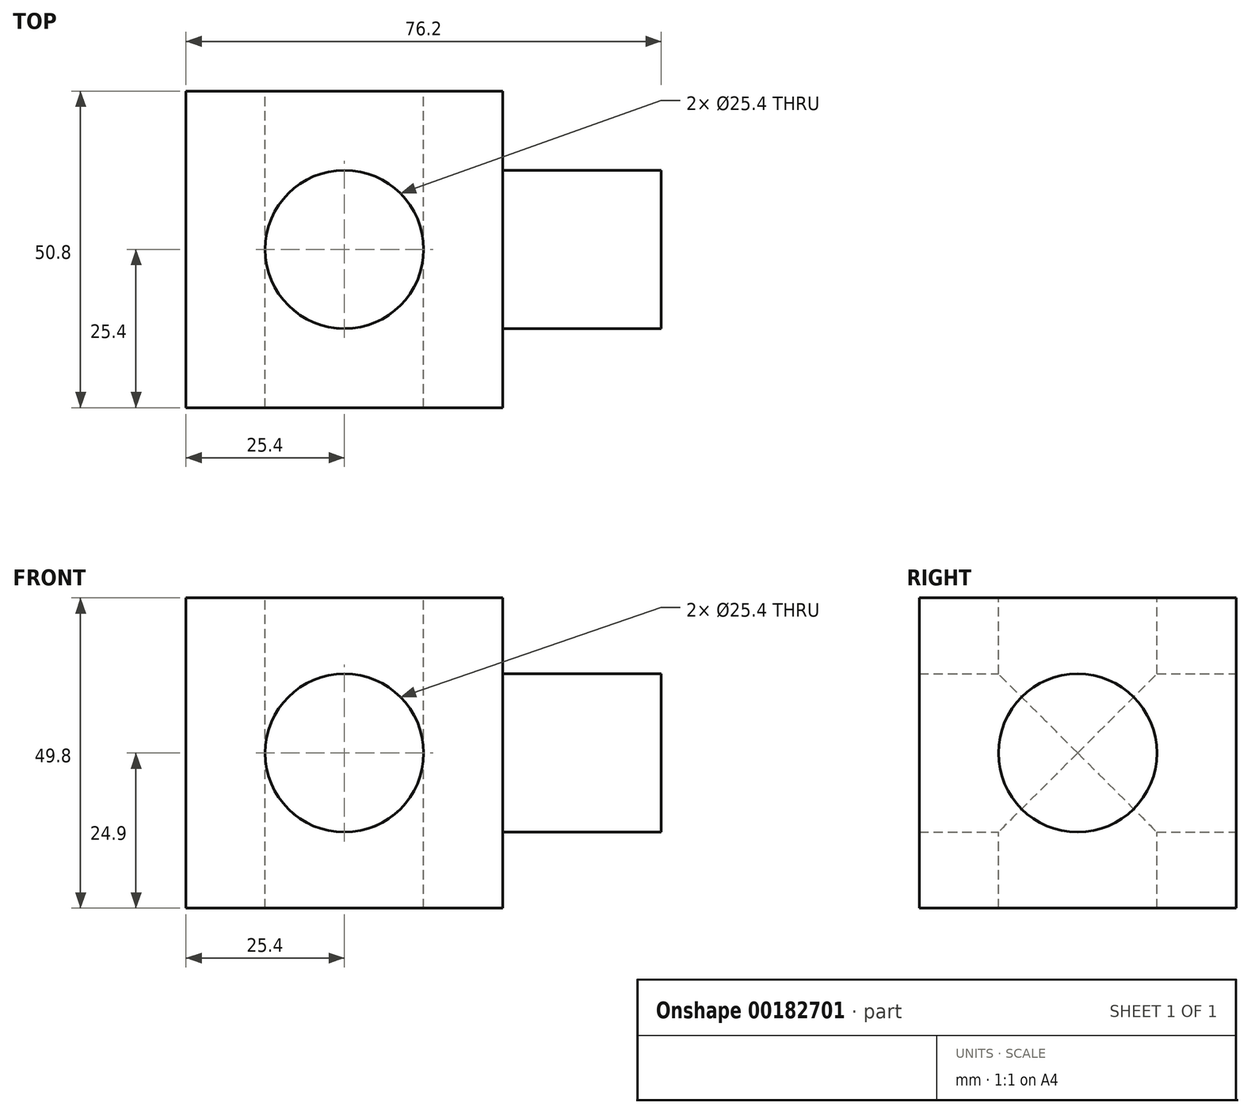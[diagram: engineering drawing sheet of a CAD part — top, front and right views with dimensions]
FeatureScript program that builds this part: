
annotation { "Feature Type Name" : "Feature", "Feature Type Description" : "" }
export const myFeature = defineFeature(function(context is Context, id is Id, definition is map)
    precondition{}
    {
        {
            var Q0;
            Q0=qCreatedBy(makeId("Front.planeOp"),FACE);
            var sketch = newSketch(context, id + "F0", { "sketchPlane" : qUnion([Q0])});
            skLineSegment(sketch, "E0.bottom", {"start": v(-25.4, 24.9) * mm, "end": v(25.4, 24.9) * mm});
            skLineSegment(sketch, "E0.top", {"start": v(-25.4, -24.9) * mm, "end": v(25.4, -24.9) * mm});
            skLineSegment(sketch, "E0.left", {"start": v(-25.4, 24.9) * mm, "end": v(-25.4, -24.9) * mm});
            skLineSegment(sketch, "E0.right", {"start": v(25.4, 24.9) * mm, "end": v(25.4, -24.9) * mm});
            skPoint(sketch, "E0.middle", {"position": v(0, 0) * mm});
            skCircle(sketch, "E1", {"center": v(0, 0) * mm, "radius": 12.7 * mm});
            skSolve(sketch);
        }
        {
            var Q0;
            Q0=makeQuery(id+"F0.imprint","IMPRINT",FACE,{"disambiguationData":[TD([[makeQuery(id+"F0.imprint","IMPRINT",EDGE,{"derivedFrom":sQuery(id+"F0.wireOp",EDGE,"E0.bottom")}),-1.0]])]});
            extrude(context, id + "F1", {"entities" : qUnion([Q0]), "endBound" : BoundingType.SYMMETRIC, "depth" : 50.8 * mm});
        }
        {
            var Q0;
            Q0=qCreatedBy(makeId("Top.planeOp"),FACE);
            cPlane(context, id + "F2", {"entities" : qUnion([Q0]), "cplaneType" : CPlaneType.OFFSET, "offset" : 25.4 * mm, "width" : 152.4 * mm, "height" : 152.4 * mm});
        }
        {
            var Q0;
            Q0=qCreatedBy(id+"F2.planeOp",FACE);
            var sketch = newSketch(context, id + "F3", { "sketchPlane" : qUnion([Q0])});
            skCircle(sketch, "E2", {"center": v(0, 0) * mm, "radius": 12.7 * mm});
            skSolve(sketch);
        }
        {
            var Q0;
            Q0=makeQuery(id+"F3.imprint","IMPRINT",FACE,{"disambiguationData":[TD([[makeQuery(id+"F3.imprint","IMPRINT",EDGE,{"derivedFrom":sQuery(id+"F3.wireOp",EDGE,"E2")}),1.0]])]});
            extrude(context, id + "F4", {"entities" : qUnion([Q0]), "operationType" : NewBodyOperationType.REMOVE, "oppositeDirection" : true, "depth" : 50.8 * mm});
        }
        {
            var Q0;
            Q0=qCreatedBy(makeId("Right.planeOp"),FACE);
            cPlane(context, id + "F5", {"entities" : qUnion([Q0]), "cplaneType" : CPlaneType.OFFSET, "offset" : 25.4 * mm, "width" : 152.4 * mm, "height" : 152.4 * mm});
        }
        {
            var Q0;
            Q0=qCreatedBy(id+"F5.planeOp",FACE);
            var sketch = newSketch(context, id + "F6", { "sketchPlane" : qUnion([Q0])});
            skCircle(sketch, "E3", {"center": v(0, 0) * mm, "radius": 12.7 * mm});
            skSolve(sketch);
        }
        {
            var Q0;
            Q0=makeQuery(id+"F6.imprint","IMPRINT",FACE,{"disambiguationData":[TD([[makeQuery(id+"F6.imprint","IMPRINT",EDGE,{"derivedFrom":sQuery(id+"F6.wireOp",EDGE,"E3")}),1.0]])]});
            extrude(context, id + "F7", {"entities" : qUnion([Q0]), "operationType" : NewBodyOperationType.ADD, "depth" : 25.4 * mm});
        }
    });
